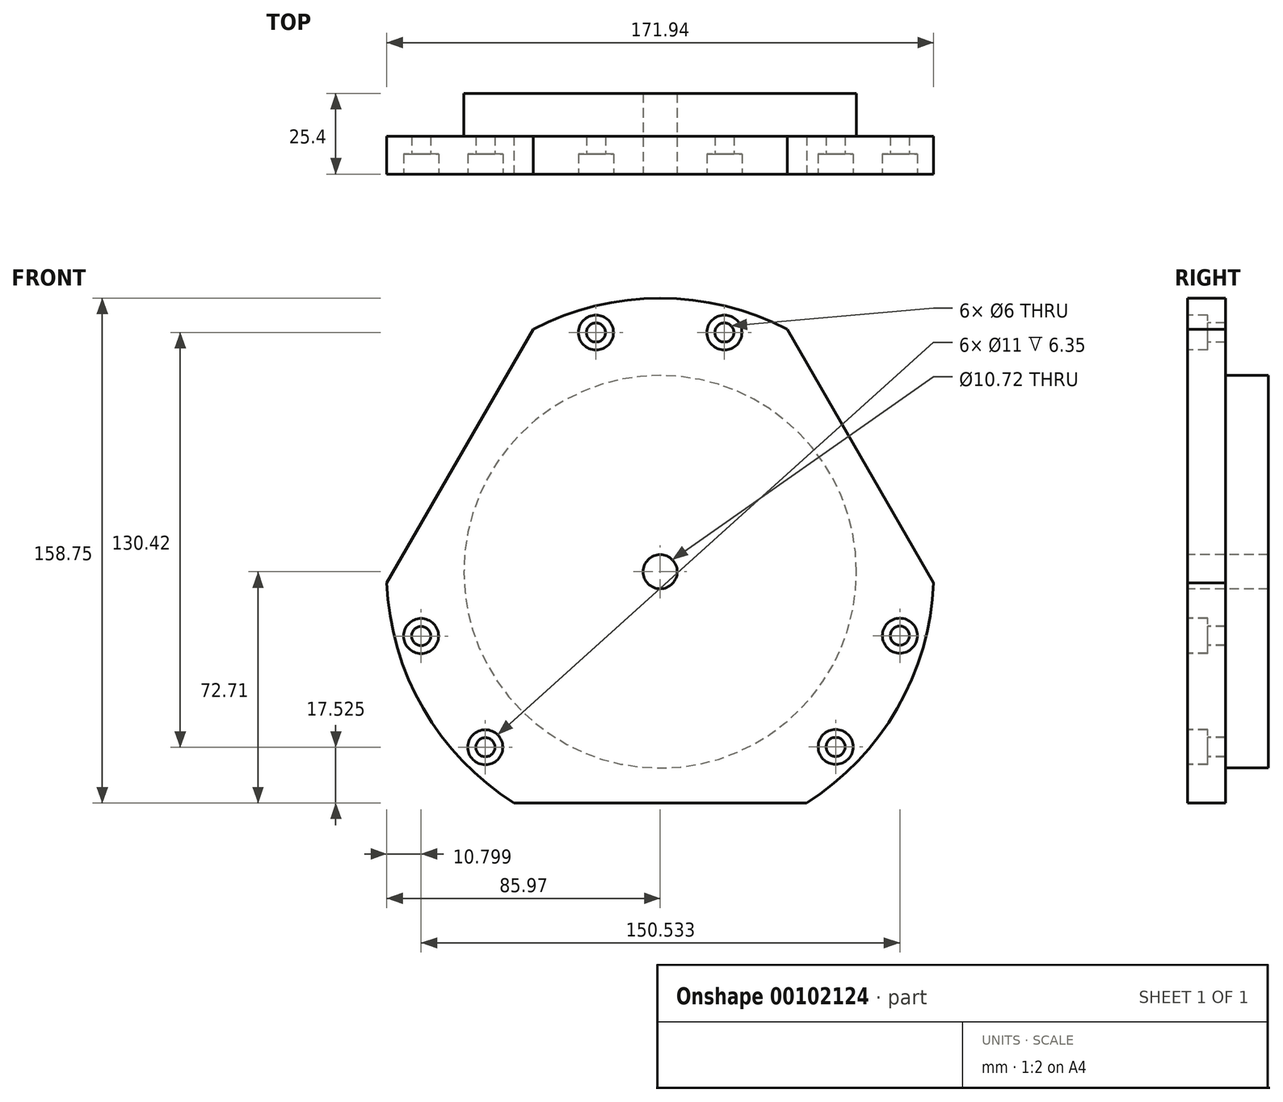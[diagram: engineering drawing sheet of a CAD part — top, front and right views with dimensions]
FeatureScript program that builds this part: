
annotation { "Feature Type Name" : "Feature", "Feature Type Description" : "" }
export const myFeature = defineFeature(function(context is Context, id is Id, definition is map)
    precondition{}
    {
        {
            var Q0;
            Q0=qCreatedBy(makeId("Front.planeOp"),FACE);
            var sketch = newSketch(context, id + "F0", { "sketchPlane" : qUnion([Q0])});
            skCircle(sketch, "E0", {"center": v(0, 0) * mm, "radius": 86.04 * mm});
            skSolve(sketch);
        }
        {
            var Q0;
            Q0=makeQuery(id+"F0.imprint","IMPRINT",FACE,{"disambiguationData":[TD([[makeQuery(id+"F0.imprint","IMPRINT",EDGE,{"derivedFrom":sQuery(id+"F0.wireOp",EDGE,"E0")}),1.0]])]});
            extrude(context, id + "F1", {"entities" : qUnion([Q0]), "depth" : 11.94 * mm});
        }
        {
            var Q0;
            Q0=makeQuery(id+"F1.opExtrude","CAP_FACE",FACE,{"disambiguationData":[OSD([sQuery(id+"F0.wireOp",EDGE,"E0")])],"isStart":true});
            var sketch = newSketch(context, id + "F2", { "sketchPlane" : qUnion([Q0])});
            skCircle(sketch, "E1", {"center": v(0, 0) * mm, "radius": 61.72 * mm});
            skSolve(sketch);
        }
        {
            var Q0;
            Q0=makeQuery(id+"F2.imprint","IMPRINT",FACE,{"disambiguationData":[TD([[makeQuery(id+"F2.imprint","IMPRINT",EDGE,{"derivedFrom":sQuery(id+"F2.wireOp",EDGE,"E1")}),1.0]])]});
            extrude(context, id + "F3", {"entities" : qUnion([Q0]), "operationType" : NewBodyOperationType.ADD, "depth" : 13.46 * mm});
        }
        {
            var Q0;
            Q0=makeQuery(id+"F1.opExtrude","CAP_FACE",FACE,{"disambiguationData":[OSD([sQuery(id+"F0.wireOp",EDGE,"E0")])],"isStart":false});
            var sketch = newSketch(context, id + "F4", { "sketchPlane" : qUnion([Q0])});
            skLineSegment(sketch, "E2", {"start": v(39.96, 76.2) * mm, "end": v(85.97, -3.5) * mm});
            skLineSegment(sketch, "E3.1.0", {"start": v(-85.97, -3.5) * mm, "end": v(-39.96, 76.2) * mm});
            skLineSegment(sketch, "E3.2.0", {"start": v(46.01, -72.7) * mm, "end": v(-46.01, -72.7) * mm});
            skPoint(sketch, "E3.center", {"position": v(0, 0) * mm});
            skSolve(sketch);
        }
        {
            var Q0;
            {var subQ0=sQuery(id+"F4.wireOp",EDGE,"E3.1.0");Q0=makeQuery(id+"F4.imprint","IMPRINT",FACE,{"disambiguationData":[TD([[makeQuery(id+"F4.imprint","IMPRINT",EDGE,{"derivedFrom":subQ0}),1.0]])]});}
            var Q1;
            {var subQ0=sQuery(id+"F4.wireOp",EDGE,"E2");Q1=makeQuery(id+"F4.imprint","IMPRINT",FACE,{"disambiguationData":[TD([[makeQuery(id+"F4.imprint","IMPRINT",EDGE,{"derivedFrom":subQ0}),1.0]])]});}
            var Q2;
            {var subQ0=sQuery(id+"F4.wireOp",EDGE,"E3.2.0");Q2=makeQuery(id+"F4.imprint","IMPRINT",FACE,{"disambiguationData":[TD([[makeQuery(id+"F4.imprint","IMPRINT",EDGE,{"derivedFrom":subQ0}),1.0]])]});}
            extrude(context, id + "F5", {"entities" : qUnion([Q0, Q1, Q2]), "operationType" : NewBodyOperationType.REMOVE, "endBound" : BoundingType.THROUGH_ALL, "oppositeDirection" : true, "depth" : 25.4 * mm});
        }
        {
            var Q0;
            Q0=makeQuery(id+"F1.opExtrude","CAP_FACE",FACE,{"disambiguationData":[OSD([sQuery(id+"F0.wireOp",EDGE,"E0")])],"isStart":false});
            var sketch = newSketch(context, id + "F6", { "sketchPlane" : qUnion([Q0])});
            skCircle(sketch, "E4", {"center": v(20.2, 75.23) * mm, "radius": 5.5 * mm});
            skCircle(sketch, "E5", {"center": v(20.2, 75.23) * mm, "radius": 3 * mm});
            skCircle(sketch, "E6.MirrorC", {"center": v(-20.2, 75.23) * mm, "radius": 5.5 * mm});
            skCircle(sketch, "E7.MirrorC", {"center": v(-20.2, 75.23) * mm, "radius": 3 * mm});
            skCircle(sketch, "E8.1.0", {"center": v(-75.17, -20.2) * mm, "radius": 5.5 * mm});
            skCircle(sketch, "E8.1.1", {"center": v(-75.17, -20.2) * mm, "radius": 3 * mm});
            skCircle(sketch, "E8.1.2", {"center": v(-54.98, -55.19) * mm, "radius": 5.5 * mm});
            skCircle(sketch, "E8.1.3", {"center": v(-54.98, -55.19) * mm, "radius": 3 * mm});
            skCircle(sketch, "E8.2.0", {"center": v(55.17, -55.08) * mm, "radius": 5.5 * mm});
            skCircle(sketch, "E8.2.1", {"center": v(55.17, -55.08) * mm, "radius": 3 * mm});
            skCircle(sketch, "E8.2.2", {"center": v(75.36, -20.1) * mm, "radius": 5.5 * mm});
            skCircle(sketch, "E8.2.3", {"center": v(75.36, -20.1) * mm, "radius": 3 * mm});
            skPoint(sketch, "E8.center", {"position": v(0.06, -0.02) * mm});
            skSolve(sketch);
        }
        {
            var Q0;
            Q0=sQuery(id+"F6.wireOp",VERTEX,"E5.center");
            var Q1;
            Q1=sQuery(id+"F6.wireOp",VERTEX,"E7.MirrorC.center");
            var Q2;
            Q2=sQuery(id+"F6.wireOp",VERTEX,"E8.1.1.center");
            var Q3;
            Q3=sQuery(id+"F6.wireOp",VERTEX,"E8.1.3.center");
            var Q4;
            Q4=sQuery(id+"F6.wireOp",VERTEX,"E8.2.1.center");
            var Q5;
            Q5=sQuery(id+"F6.wireOp",VERTEX,"E8.2.3.center");
            var Q6;
            Q6=makeQuery(id+"F1.opExtrude","SWEPT_BODY",BODY,{"disambiguationData":[OSD([sQuery(id+"F0.wireOp",EDGE,"E0")])]});
            hole(context, id + "F7", {"style" : HoleStyle.C_BORE, "endStyle" : HoleEndStyle.THROUGH, "holeDiameter" : 6 * mm, "cBoreDiameter" : 11 * mm, "cBoreDepth" : 6.35 * mm, "locations" : qUnion([Q0, Q1, Q2, Q3, Q4, Q5]), "scope" : qUnion([Q6]), "isTappedThrough" : true});
        }
        {
            var Q0;
            Q0=makeQuery(id+"F1.opExtrude","CAP_FACE",FACE,{"disambiguationData":[OSD([sQuery(id+"F0.wireOp",EDGE,"E0")])],"isStart":false});
            var sketch = newSketch(context, id + "F8", { "sketchPlane" : qUnion([Q0])});
            skCircle(sketch, "E9", {"center": v(0, 0) * mm, "radius": 6.35 * mm});
            skSolve(sketch);
        }
        {
            var Q0;
            Q0=sQuery(id+"F8.wireOp",VERTEX,"E9.center");
            var Q1;
            Q1=makeQuery(id+"F1.opExtrude","SWEPT_BODY",BODY,{"disambiguationData":[OSD([sQuery(id+"F0.wireOp",EDGE,"E0")])]});
            hole(context, id + "F9", {"style" : HoleStyle.SIMPLE, "endStyle" : HoleEndStyle.THROUGH, "standardTappedOrClearance" : lookupTablePath({ "standard" : "ANSI", "engagement" : "75%", "pitch" : "13 tpi", "size" : "1/2", "type" : "Tapped" }), "standardBlindInLast" : lookupTablePath({ "standard" : "ANSI", "engagement" : "75%", "pitch" : "13 tpi", "size" : "1/2", "type" : "Tapped" }), "holeDiameter" : 10.72 * mm, "locations" : qUnion([Q0]), "scope" : qUnion([Q1]), "isTappedThrough" : true, "majorDiameter" : 12.7 * mm, "showTappedDepth" : true});
        }
    });
